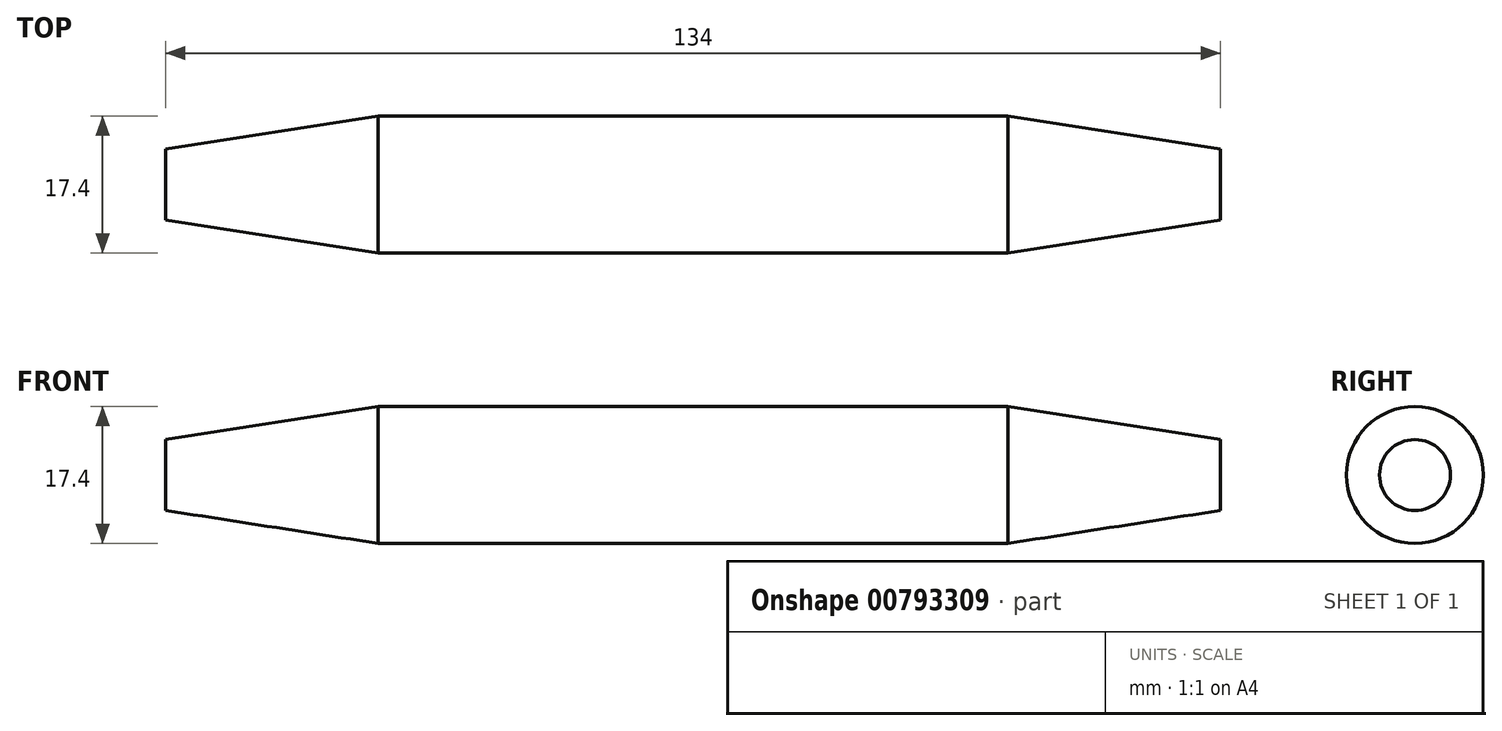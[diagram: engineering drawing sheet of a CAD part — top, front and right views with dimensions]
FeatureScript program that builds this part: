
annotation { "Feature Type Name" : "Feature", "Feature Type Description" : "" }
export const myFeature = defineFeature(function(context is Context, id is Id, definition is map)
    precondition{}
    {
        {
            var Q0;
            Q0=qCreatedBy(makeId("Front.planeOp"),FACE);
            var sketch = newSketch(context, id + "F0", { "sketchPlane" : qUnion([Q0])});
            skLineSegment(sketch, "E0", {"start": v(0, 0) * mm, "end": v(0, 4.5) * mm});
            skLineSegment(sketch, "E1", {"start": v(0, 4.5) * mm, "end": v(27, 8.7) * mm});
            skLineSegment(sketch, "E2", {"start": v(27, 8.7) * mm, "end": v(107, 8.7) * mm});
            skLineSegment(sketch, "E3", {"start": v(134, 0) * mm, "end": v(134, 4.5) * mm});
            skLineSegment(sketch, "E4", {"start": v(134, 4.5) * mm, "end": v(107, 8.7) * mm});
            skLineSegment(sketch, "E5", {"start": v(134, 0) * mm, "end": v(0, 0) * mm});
            skSolve(sketch);
        }
        {
            var Q0;
            Q0 = qSketchRegion(id + "F0", true);
            var Q1;
            Q1=sQuery(id+"F0.wireOp",EDGE,"E5");
            revolve(context, id + "F1", {"surfaceOperationType" : NewSurfaceOperationType.NEW, "entities" : qUnion([Q0]), "axis" : qUnion([Q1]), "revolveType" : RevolveType.FULL});
        }
    });
